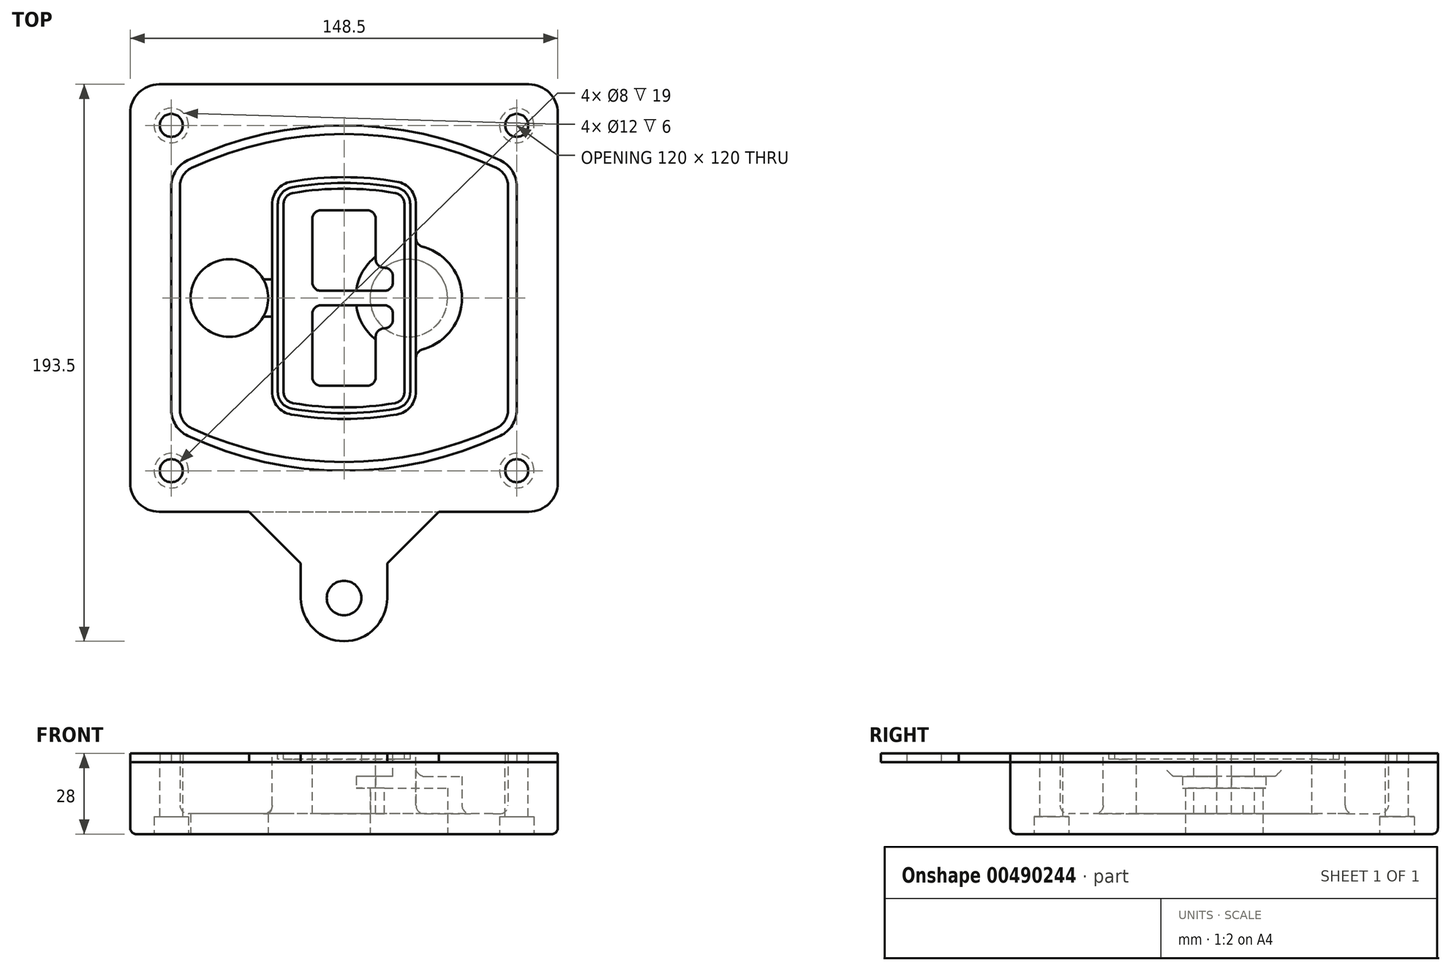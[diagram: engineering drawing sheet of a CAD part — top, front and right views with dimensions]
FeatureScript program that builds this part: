
annotation { "Feature Type Name" : "Feature", "Feature Type Description" : "" }
export const myFeature = defineFeature(function(context is Context, id is Id, definition is map)
    precondition{}
    {
        {
            var Q0;
            Q0=qCreatedBy(makeId("Top.planeOp"),FACE);
            var sketch = newSketch(context, id + "F0", { "sketchPlane" : qUnion([Q0])});
            skPoint(sketch, "E0.rect.middle", {"position": v(0, 0) * mm});
            skLineSegment(sketch, "E1.bottom", {"start": v(-64.25, -74.25) * mm, "end": v(64.25, -74.25) * mm});
            skLineSegment(sketch, "E1.top", {"start": v(-64.25, 74.25) * mm, "end": v(64.25, 74.25) * mm});
            skLineSegment(sketch, "E1.left", {"start": v(-74.25, -64.25) * mm, "end": v(-74.25, 64.25) * mm});
            skLineSegment(sketch, "E1.right", {"start": v(74.25, -64.25) * mm, "end": v(74.25, 64.25) * mm});
            skLineSegment(sketch, "E2", {"start": v(-74.25, 74.25) * mm, "end": v(74.25, -74.25) * mm, "construction": true});
            skLineSegment(sketch, "E3", {"start": v(74.25, 74.25) * mm, "end": v(-74.25, -74.25) * mm, "construction": true});
            skCircle(sketch, "E4", {"center": v(-60, 60) * mm, "radius": 4 * mm});
            skCircle(sketch, "E5", {"center": v(60, 60) * mm, "radius": 4 * mm});
            skCircle(sketch, "E6", {"center": v(60, -60) * mm, "radius": 4 * mm});
            skCircle(sketch, "E7", {"center": v(-60, -60) * mm, "radius": 4 * mm});
            skLineSegment(sketch, "E8", {"start": v(-60, 60) * mm, "end": v(60, 60) * mm, "construction": true});
            skLineSegment(sketch, "E9", {"start": v(60, 60) * mm, "end": v(60, -60) * mm, "construction": true});
            skLineSegment(sketch, "E10", {"start": v(60, -60) * mm, "end": v(-60, -60) * mm, "construction": true});
            skLineSegment(sketch, "E11", {"start": v(-60, -60) * mm, "end": v(-60, 60) * mm, "construction": true});
            skLineSegment(sketch, "E12", {"start": v(-60, 38.83) * mm, "end": v(-60, -38.83) * mm});
            skLineSegment(sketch, "E13", {"start": v(60, 38.83) * mm, "end": v(60, -38.83) * mm});
            skArc(sketch, "E14", {"start": v(54.26, 47.88) * mm, "mid": v(0, 60) * mm, "end": v(-54.26, 47.88) * mm});
            skArc(sketch, "E15", {"start": v(-54.26, -47.88) * mm, "mid": v(0, -60) * mm, "end": v(54.26, -47.88) * mm});
            skLineSegment(sketch, "E16", {"start": v(-60, 0) * mm, "end": v(60, 0) * mm, "construction": true});
            skPoint(sketch, "E17.visualSharp", {"position": v(-60, -45) * mm});
            skArc(sketch, "E17.filletArc", {"start": v(-60, -38.83) * mm, "mid": v(-58.44, -44.2) * mm, "end": v(-54.26, -47.88) * mm});
            skPoint(sketch, "E18.visualSharp", {"position": v(-60, 45) * mm});
            skArc(sketch, "E18.filletArc", {"start": v(-54.26, 47.88) * mm, "mid": v(-58.44, 44.2) * mm, "end": v(-60, 38.83) * mm});
            skPoint(sketch, "E19.visualSharp", {"position": v(60, 45) * mm});
            skArc(sketch, "E19.filletArc", {"start": v(60, 38.83) * mm, "mid": v(58.44, 44.2) * mm, "end": v(54.26, 47.88) * mm});
            skPoint(sketch, "E20.visualSharp", {"position": v(60, -45) * mm});
            skArc(sketch, "E20.filletArc", {"start": v(54.26, -47.88) * mm, "mid": v(58.44, -44.2) * mm, "end": v(60, -38.83) * mm});
            skPoint(sketch, "E21.visualSharp", {"position": v(-74.25, 74.25) * mm});
            skArc(sketch, "E21.filletArc", {"start": v(-64.25, 74.25) * mm, "mid": v(-71.32, 71.32) * mm, "end": v(-74.25, 64.25) * mm});
            skPoint(sketch, "E22.visualSharp", {"position": v(74.25, 74.25) * mm});
            skArc(sketch, "E22.filletArc", {"start": v(74.25, 64.25) * mm, "mid": v(71.32, 71.32) * mm, "end": v(64.25, 74.25) * mm});
            skPoint(sketch, "E23.visualSharp", {"position": v(74.25, -74.25) * mm});
            skArc(sketch, "E23.filletArc", {"start": v(64.25, -74.25) * mm, "mid": v(71.32, -71.32) * mm, "end": v(74.25, -64.25) * mm});
            skPoint(sketch, "E24.visualSharp", {"position": v(-74.25, -74.25) * mm});
            skArc(sketch, "E24.filletArc", {"start": v(-74.25, -64.25) * mm, "mid": v(-71.32, -71.32) * mm, "end": v(-64.25, -74.25) * mm});
            skArc(sketch, "E25.0", {"start": v(57, 38.83) * mm, "mid": v(55.9, 42.58) * mm, "end": v(52.98, 45.17) * mm});
            skLineSegment(sketch, "E25.1", {"start": v(57, 38.83) * mm, "end": v(57, -38.83) * mm});
            skArc(sketch, "E25.2", {"start": v(52.98, -45.17) * mm, "mid": v(55.9, -42.58) * mm, "end": v(57, -38.83) * mm});
            skArc(sketch, "E25.3", {"start": v(-52.98, -45.17) * mm, "mid": v(0, -57) * mm, "end": v(52.98, -45.17) * mm});
            skArc(sketch, "E25.4", {"start": v(-57, -38.83) * mm, "mid": v(-55.9, -42.58) * mm, "end": v(-52.98, -45.17) * mm});
            skArc(sketch, "E25.5", {"start": v(52.98, 45.17) * mm, "mid": v(0, 57) * mm, "end": v(-52.98, 45.17) * mm});
            skLineSegment(sketch, "E25.6", {"start": v(-57, 38.83) * mm, "end": v(-57, -38.83) * mm});
            skArc(sketch, "E25.7", {"start": v(-52.98, 45.17) * mm, "mid": v(-55.9, 42.58) * mm, "end": v(-57, 38.83) * mm});
            skArc(sketch, "E26.0", {"start": v(-55.96, 51.5) * mm, "mid": v(-61.82, 46.33) * mm, "end": v(-64, 38.83) * mm});
            skArc(sketch, "E26.1", {"start": v(55.96, 51.5) * mm, "mid": v(0, 64) * mm, "end": v(-55.96, 51.5) * mm});
            skArc(sketch, "E26.2", {"start": v(64, 38.83) * mm, "mid": v(61.82, 46.33) * mm, "end": v(55.96, 51.5) * mm});
            skLineSegment(sketch, "E26.3", {"start": v(64, 38.83) * mm, "end": v(64, -38.83) * mm});
            skArc(sketch, "E26.4", {"start": v(55.96, -51.5) * mm, "mid": v(61.82, -46.33) * mm, "end": v(64, -38.83) * mm});
            skLineSegment(sketch, "E26.5", {"start": v(-64, 38.83) * mm, "end": v(-64, -38.83) * mm});
            skArc(sketch, "E26.6", {"start": v(-55.96, -51.5) * mm, "mid": v(0, -64) * mm, "end": v(55.96, -51.5) * mm});
            skArc(sketch, "E26.7", {"start": v(-64, -38.83) * mm, "mid": v(-61.82, -46.33) * mm, "end": v(-55.96, -51.5) * mm});
            skSolve(sketch);
        }
        {
            var Q0;
            Q0=makeQuery(id+"F0.imprint","IMPRINT",FACE,{"disambiguationData":[TD([[makeQuery(id+"F0.imprint","IMPRINT",EDGE,{"derivedFrom":sQuery(id+"F0.wireOp",EDGE,"E1.bottom")}),1.0]])]});
            var Q1;
            Q1=makeQuery(id+"F0.imprint","IMPRINT",FACE,{"disambiguationData":[TD([[makeQuery(id+"F0.imprint","IMPRINT",EDGE,{"derivedFrom":sQuery(id+"F0.wireOp",EDGE,"E12")}),1.0]])]});
            var Q2;
            Q2=makeQuery(id+"F0.imprint","IMPRINT",FACE,{"disambiguationData":[TD([[makeQuery(id+"F0.imprint","IMPRINT",EDGE,{"derivedFrom":sQuery(id+"F0.wireOp",EDGE,"E25.0")}),1.0]])]});
            var Q3;
            Q3=makeQuery(id+"F0.imprint","IMPRINT",FACE,{"disambiguationData":[TD([[makeQuery(id+"F0.imprint","IMPRINT",EDGE,{"derivedFrom":sQuery(id+"F0.wireOp",EDGE,"E12")}),-1.0]])]});
            extrude(context, id + "F1", {"entities" : qUnion([Q0, Q1, Q2, Q3]), "oppositeDirection" : true, "depth" : 25 * mm});
        }
        {
            var Q0;
            Q0=makeQuery(id+"F0.imprint","IMPRINT",FACE,{"disambiguationData":[TD([[makeQuery(id+"F0.imprint","IMPRINT",EDGE,{"derivedFrom":sQuery(id+"F0.wireOp",EDGE,"E12")}),1.0]])]});
            extrude(context, id + "F2", {"entities" : qUnion([Q0]), "operationType" : NewBodyOperationType.ADD, "depth" : 3 * mm});
        }
        {
            var Q0;
            Q0=makeQuery(id+"F0.imprint","IMPRINT",FACE,{"disambiguationData":[TD([[makeQuery(id+"F0.imprint","IMPRINT",EDGE,{"derivedFrom":sQuery(id+"F0.wireOp",EDGE,"E25.0")}),1.0]])]});
            extrude(context, id + "F3", {"entities" : qUnion([Q0]), "operationType" : NewBodyOperationType.REMOVE, "oppositeDirection" : true, "depth" : 18 * mm});
        }
        {
            var Q0;
            Q0=makeQuery(id+"F2.opExtrude","CAP_FACE",FACE,{"disambiguationData":[OSD([sQuery(id+"F0.wireOp",EDGE,"E12"),sQuery(id+"F0.wireOp",EDGE,"E13"),sQuery(id+"F0.wireOp",EDGE,"E14"),sQuery(id+"F0.wireOp",EDGE,"E15"),sQuery(id+"F0.wireOp",EDGE,"E17.filletArc"),sQuery(id+"F0.wireOp",EDGE,"E18.filletArc"),sQuery(id+"F0.wireOp",EDGE,"E19.filletArc"),sQuery(id+"F0.wireOp",EDGE,"E20.filletArc"),sQuery(id+"F0.wireOp",EDGE,"E25.0"),sQuery(id+"F0.wireOp",EDGE,"E25.1"),sQuery(id+"F0.wireOp",EDGE,"E25.2"),sQuery(id+"F0.wireOp",EDGE,"E25.3"),sQuery(id+"F0.wireOp",EDGE,"E25.4"),sQuery(id+"F0.wireOp",EDGE,"E25.5"),sQuery(id+"F0.wireOp",EDGE,"E25.6"),sQuery(id+"F0.wireOp",EDGE,"E25.7")])],"isStart":false});
            var sketch = newSketch(context, id + "F4", { "sketchPlane" : qUnion([Q0])});
            skArc(sketch, "E27.0", {"start": v(-18.34, -40.45) * mm, "mid": v(0, -42) * mm, "end": v(18.34, -40.45) * mm});
            skArc(sketch, "E28.0", {"start": v(18.34, 40.45) * mm, "mid": v(0, 42) * mm, "end": v(-18.34, 40.45) * mm});
            skLineSegment(sketch, "E29", {"start": v(-25, 32.57) * mm, "end": v(-25, -32.57) * mm});
            skLineSegment(sketch, "E30", {"start": v(25, 32.57) * mm, "end": v(25, -32.57) * mm});
            skLineSegment(sketch, "E31", {"start": v(-25, 39.1) * mm, "end": v(25, 39.1) * mm, "construction": true});
            skLineSegment(sketch, "E32", {"start": v(-25, -39.1) * mm, "end": v(25, -39.1) * mm, "construction": true});
            skPoint(sketch, "E33.visualSharp", {"position": v(-25, 39.1) * mm});
            skArc(sketch, "E33.filletArc", {"start": v(-18.34, 40.45) * mm, "mid": v(-23.11, 37.73) * mm, "end": v(-25, 32.57) * mm});
            skPoint(sketch, "E34.visualSharp", {"position": v(25, 39.1) * mm});
            skArc(sketch, "E34.filletArc", {"start": v(25, 32.57) * mm, "mid": v(23.11, 37.73) * mm, "end": v(18.34, 40.45) * mm});
            skPoint(sketch, "E35.visualSharp", {"position": v(25, -39.1) * mm});
            skArc(sketch, "E35.filletArc", {"start": v(18.34, -40.45) * mm, "mid": v(23.11, -37.73) * mm, "end": v(25, -32.57) * mm});
            skPoint(sketch, "E36.visualSharp", {"position": v(-25, -39.1) * mm});
            skArc(sketch, "E36.filletArc", {"start": v(-25, -32.57) * mm, "mid": v(-23.11, -37.73) * mm, "end": v(-18.34, -40.45) * mm});
            skArc(sketch, "E37.0", {"start": v(52.98, 45.17) * mm, "mid": v(0, 57) * mm, "end": v(-52.98, 45.17) * mm});
            skArc(sketch, "E37.1", {"start": v(-52.98, 45.17) * mm, "mid": v(-55.9, 42.58) * mm, "end": v(-57, 38.83) * mm});
            skLineSegment(sketch, "E37.2", {"start": v(-57, 38.83) * mm, "end": v(-57, -38.83) * mm});
            skArc(sketch, "E37.3", {"start": v(-57, -38.83) * mm, "mid": v(-55.9, -42.58) * mm, "end": v(-52.98, -45.17) * mm});
            skArc(sketch, "E37.4", {"start": v(-52.98, -45.17) * mm, "mid": v(0, -57) * mm, "end": v(52.98, -45.17) * mm});
            skArc(sketch, "E37.5", {"start": v(52.98, -45.17) * mm, "mid": v(55.9, -42.58) * mm, "end": v(57, -38.83) * mm});
            skLineSegment(sketch, "E37.6", {"start": v(57, 38.83) * mm, "end": v(57, -38.83) * mm});
            skArc(sketch, "E37.7", {"start": v(57, 38.83) * mm, "mid": v(55.9, 42.58) * mm, "end": v(52.98, 45.17) * mm});
            skLineSegment(sketch, "E38.0", {"start": v(23, 32.57) * mm, "end": v(23, -32.57) * mm});
            skArc(sketch, "E38.1", {"start": v(18, -38.48) * mm, "mid": v(21.58, -36.44) * mm, "end": v(23, -32.57) * mm});
            skArc(sketch, "E38.2", {"start": v(-18, -38.48) * mm, "mid": v(0, -40) * mm, "end": v(18, -38.48) * mm});
            skArc(sketch, "E38.3", {"start": v(-23, -32.57) * mm, "mid": v(-21.58, -36.44) * mm, "end": v(-18, -38.48) * mm});
            skLineSegment(sketch, "E38.4", {"start": v(-23, 32.57) * mm, "end": v(-23, -32.57) * mm});
            skArc(sketch, "E38.5", {"start": v(23, 32.57) * mm, "mid": v(21.58, 36.44) * mm, "end": v(18, 38.48) * mm});
            skArc(sketch, "E38.6", {"start": v(-18, 38.48) * mm, "mid": v(-21.58, 36.44) * mm, "end": v(-23, 32.57) * mm});
            skArc(sketch, "E38.7", {"start": v(18, 38.48) * mm, "mid": v(0, 40) * mm, "end": v(-18, 38.48) * mm});
            skArc(sketch, "E39.0", {"start": v(21, 32.57) * mm, "mid": v(20.06, 35.15) * mm, "end": v(17.67, 36.5) * mm});
            skLineSegment(sketch, "E39.1", {"start": v(21, 32.57) * mm, "end": v(21, -32.57) * mm});
            skArc(sketch, "E39.2", {"start": v(17.67, -36.5) * mm, "mid": v(20.06, -35.15) * mm, "end": v(21, -32.57) * mm});
            skArc(sketch, "E39.3", {"start": v(-17.67, -36.5) * mm, "mid": v(0, -38) * mm, "end": v(17.67, -36.5) * mm});
            skArc(sketch, "E39.4", {"start": v(-21, -32.57) * mm, "mid": v(-20.06, -35.15) * mm, "end": v(-17.67, -36.5) * mm});
            skArc(sketch, "E39.5", {"start": v(17.67, 36.5) * mm, "mid": v(0, 38) * mm, "end": v(-17.67, 36.5) * mm});
            skLineSegment(sketch, "E39.6", {"start": v(-21, 32.57) * mm, "end": v(-21, -32.57) * mm});
            skArc(sketch, "E39.7", {"start": v(-17.67, 36.5) * mm, "mid": v(-20.06, 35.15) * mm, "end": v(-21, 32.57) * mm});
            skLineSegment(sketch, "E40", {"start": v(-25, 0) * mm, "end": v(25, 0) * mm, "construction": true});
            skLineSegment(sketch, "E41", {"start": v(-11, 5.5) * mm, "end": v(-11, 27.5) * mm});
            skLineSegment(sketch, "E42", {"start": v(-8, 30.5) * mm, "end": v(8, 30.5) * mm});
            skLineSegment(sketch, "E43", {"start": v(11, 27.5) * mm, "end": v(11, 13.5) * mm});
            skLineSegment(sketch, "E44", {"start": v(14, 10.5) * mm, "end": v(14, 10.5) * mm});
            skLineSegment(sketch, "E45", {"start": v(17, 7.5) * mm, "end": v(17, 5.5) * mm});
            skLineSegment(sketch, "E46", {"start": v(14, 2.5) * mm, "end": v(-8, 2.5) * mm});
            skPoint(sketch, "E47.visualSharp", {"position": v(-11, 30.5) * mm});
            skArc(sketch, "E47.filletArc", {"start": v(-8, 30.5) * mm, "mid": v(-10.12, 29.62) * mm, "end": v(-11, 27.5) * mm});
            skPoint(sketch, "E48.visualSharp", {"position": v(11, 30.5) * mm});
            skArc(sketch, "E48.filletArc", {"start": v(11, 27.5) * mm, "mid": v(10.12, 29.62) * mm, "end": v(8, 30.5) * mm});
            skPoint(sketch, "E49.visualSharp", {"position": v(11, 10.5) * mm});
            skArc(sketch, "E49.filletArc", {"start": v(11, 13.5) * mm, "mid": v(11.88, 11.38) * mm, "end": v(14, 10.5) * mm});
            skPoint(sketch, "E50.visualSharp", {"position": v(17, 10.5) * mm});
            skArc(sketch, "E50.filletArc", {"start": v(17, 7.5) * mm, "mid": v(16.12, 9.62) * mm, "end": v(14, 10.5) * mm});
            skPoint(sketch, "E51.visualSharp", {"position": v(17, 2.5) * mm});
            skArc(sketch, "E51.filletArc", {"start": v(14, 2.5) * mm, "mid": v(16.12, 3.38) * mm, "end": v(17, 5.5) * mm});
            skPoint(sketch, "E52.visualSharp", {"position": v(-11, 2.5) * mm});
            skArc(sketch, "E52.filletArc", {"start": v(-11, 5.5) * mm, "mid": v(-10.12, 3.38) * mm, "end": v(-8, 2.5) * mm});
            skLineSegment(sketch, "E53.0.MirrorCS", {"start": v(14, -2.5) * mm, "end": v(-8, -2.5) * mm});
            skArc(sketch, "E54.0.MirrorCS", {"start": v(-11, -5.5) * mm, "mid": v(-10.12, -3.38) * mm, "end": v(-8, -2.5) * mm});
            skLineSegment(sketch, "E55.0.MirrorCS", {"start": v(-11, -5.5) * mm, "end": v(-11, -27.5) * mm});
            skArc(sketch, "E56.0.MirrorCS", {"start": v(-8, -30.5) * mm, "mid": v(-10.12, -29.62) * mm, "end": v(-11, -27.5) * mm});
            skLineSegment(sketch, "E57.0.MirrorCS", {"start": v(-8, -30.5) * mm, "end": v(8, -30.5) * mm});
            skArc(sketch, "E58.0.MirrorCS", {"start": v(11, -27.5) * mm, "mid": v(10.12, -29.62) * mm, "end": v(8, -30.5) * mm});
            skLineSegment(sketch, "E59.0.MirrorCS", {"start": v(11, -27.5) * mm, "end": v(11, -13.5) * mm});
            skArc(sketch, "E60.0.MirrorCS", {"start": v(11, -13.5) * mm, "mid": v(11.88, -11.38) * mm, "end": v(14, -10.5) * mm});
            skArc(sketch, "E61.0.MirrorCS", {"start": v(17, -7.5) * mm, "mid": v(16.12, -9.62) * mm, "end": v(14, -10.5) * mm});
            skLineSegment(sketch, "E62.0.MirrorCS", {"start": v(17, -7.5) * mm, "end": v(17, -5.5) * mm});
            skArc(sketch, "E63.0.MirrorCS", {"start": v(14, -2.5) * mm, "mid": v(16.12, -3.38) * mm, "end": v(17, -5.5) * mm});
            skSolve(sketch);
        }
        {
            var Q0;
            Q0=makeQuery(id+"F4.imprint","IMPRINT",FACE,{"disambiguationData":[TD([[makeQuery(id+"F4.imprint","IMPRINT",EDGE,{"derivedFrom":sQuery(id+"F4.wireOp",EDGE,"E27.0")}),1.0]])]});
            var Q1;
            Q1=makeQuery(id+"F4.imprint","IMPRINT",FACE,{"disambiguationData":[TD([[makeQuery(id+"F4.imprint","IMPRINT",EDGE,{"derivedFrom":sQuery(id+"F4.wireOp",EDGE,"E38.0")}),-1.0]])]});
            var Q2;
            Q2=makeQuery(id+"F4.imprint","IMPRINT",FACE,{"disambiguationData":[TD([[makeQuery(id+"F4.imprint","IMPRINT",EDGE,{"derivedFrom":sQuery(id+"F4.wireOp",EDGE,"E39.0")}),1.0]])]});
            extrude(context, id + "F5", {"entities" : qUnion([Q0, Q1, Q2]), "operationType" : NewBodyOperationType.ADD, "endBound" : BoundingType.UP_TO_NEXT, "oppositeDirection" : true, "depth" : 25 * mm});
        }
        {
            var Q0;
            Q0=makeQuery(id+"F4.imprint","IMPRINT",FACE,{"disambiguationData":[TD([[makeQuery(id+"F4.imprint","IMPRINT",EDGE,{"derivedFrom":sQuery(id+"F4.wireOp",EDGE,"E38.0")}),-1.0]])]});
            extrude(context, id + "F6", {"entities" : qUnion([Q0]), "operationType" : NewBodyOperationType.REMOVE, "oppositeDirection" : true, "depth" : 2 * mm});
        }
        {
            var Q0;
            Q0=makeQuery(id+"F1.opExtrude","CAP_FACE",FACE,{"disambiguationData":[OSD([sQuery(id+"F0.wireOp",EDGE,"E1.bottom"),sQuery(id+"F0.wireOp",EDGE,"E1.top"),sQuery(id+"F0.wireOp",EDGE,"E1.left"),sQuery(id+"F0.wireOp",EDGE,"E1.right"),sQuery(id+"F0.wireOp",EDGE,"E4"),sQuery(id+"F0.wireOp",EDGE,"E5"),sQuery(id+"F0.wireOp",EDGE,"E6"),sQuery(id+"F0.wireOp",EDGE,"E7"),sQuery(id+"F0.wireOp",EDGE,"E21.filletArc"),sQuery(id+"F0.wireOp",EDGE,"E22.filletArc"),sQuery(id+"F0.wireOp",EDGE,"E23.filletArc"),sQuery(id+"F0.wireOp",EDGE,"E24.filletArc")])],"isStart":false});
            var sketch = newSketch(context, id + "F7", { "sketchPlane" : qUnion([Q0])});
            skCircle(sketch, "E64", {"center": v(22.5, 0) * mm, "radius": 13.47 * mm});
            skCircle(sketch, "E65", {"center": v(-39.81, 0) * mm, "radius": 13.47 * mm});
            skLineSegment(sketch, "E66", {"start": v(74.25, 0) * mm, "end": v(-74.25, 0) * mm});
            skCircle(sketch, "E67", {"center": v(22.5, 0) * mm, "radius": 18.47 * mm});
            skCircle(sketch, "E68", {"center": v(60, -60) * mm, "radius": 6 * mm});
            skCircle(sketch, "E69", {"center": v(-60, -60) * mm, "radius": 6 * mm});
            skCircle(sketch, "E70", {"center": v(-60, 60) * mm, "radius": 6 * mm});
            skCircle(sketch, "E71", {"center": v(60, 60) * mm, "radius": 6 * mm});
            skSolve(sketch);
        }
        {
            var Q0;
            {var subQ1=sQuery(id+"F7.wireOp",EDGE,"E66");var subQ4=sQuery(id+"F7.wireOp",EDGE,"E64");var subQ6=makeQuery(id+"F7.imprint","INTERSECT",VERTEX,{"disambiguationData":[OD(0.0)],"derivedFrom":[subQ4,subQ1]});Q0=makeQuery(id+"F7.imprint","IMPRINT",FACE,{"disambiguationData":[TD([[makeQuery(id+"F7.imprint","IMPRINT",EDGE,{"disambiguationData":[TD([[subQ6,-1.0]])],"derivedFrom":subQ4}),-1.0]])]});}
            var Q1;
            {var subQ0=sQuery(id+"F7.wireOp",EDGE,"E66");var subQ1=sQuery(id+"F7.wireOp",EDGE,"E64");var subQ3=makeQuery(id+"F7.imprint","INTERSECT",VERTEX,{"disambiguationData":[OD(0.0)],"derivedFrom":[subQ1,subQ0]});Q1=makeQuery(id+"F7.imprint","IMPRINT",FACE,{"disambiguationData":[TD([[makeQuery(id+"F7.imprint","IMPRINT",EDGE,{"disambiguationData":[TD([[subQ3,-1.0]])],"derivedFrom":subQ1}),1.0]])]});}
            var Q2;
            {var subQ0=sQuery(id+"F7.wireOp",EDGE,"E66");var subQ1=sQuery(id+"F7.wireOp",EDGE,"E64");var subQ3=makeQuery(id+"F7.imprint","INTERSECT",VERTEX,{"disambiguationData":[OD(0.0)],"derivedFrom":[subQ1,subQ0]});Q2=makeQuery(id+"F7.imprint","IMPRINT",FACE,{"disambiguationData":[TD([[makeQuery(id+"F7.imprint","IMPRINT",EDGE,{"disambiguationData":[TD([[subQ3,1.0]])],"derivedFrom":subQ1}),1.0]])]});}
            var Q3;
            {var subQ1=sQuery(id+"F7.wireOp",EDGE,"E66");var subQ4=sQuery(id+"F7.wireOp",EDGE,"E64");var subQ6=makeQuery(id+"F7.imprint","INTERSECT",VERTEX,{"disambiguationData":[OD(0.0)],"derivedFrom":[subQ4,subQ1]});Q3=makeQuery(id+"F7.imprint","IMPRINT",FACE,{"disambiguationData":[TD([[makeQuery(id+"F7.imprint","IMPRINT",EDGE,{"disambiguationData":[TD([[subQ6,1.0]])],"derivedFrom":subQ4}),-1.0]])]});}
            extrude(context, id + "F8", {"entities" : qUnion([Q0, Q1, Q2, Q3]), "operationType" : NewBodyOperationType.ADD, "oppositeDirection" : true, "depth" : 20 * mm});
        }
        {
            var Q0;
            {var subQ0=sQuery(id+"F7.wireOp",EDGE,"E66");var subQ1=sQuery(id+"F7.wireOp",EDGE,"E64");var subQ3=makeQuery(id+"F7.imprint","INTERSECT",VERTEX,{"disambiguationData":[OD(0.0)],"derivedFrom":[subQ1,subQ0]});Q0=makeQuery(id+"F7.imprint","IMPRINT",FACE,{"disambiguationData":[TD([[makeQuery(id+"F7.imprint","IMPRINT",EDGE,{"disambiguationData":[TD([[subQ3,-1.0]])],"derivedFrom":subQ1}),1.0]])]});}
            var Q1;
            {var subQ0=sQuery(id+"F7.wireOp",EDGE,"E66");var subQ1=sQuery(id+"F7.wireOp",EDGE,"E64");var subQ3=makeQuery(id+"F7.imprint","INTERSECT",VERTEX,{"disambiguationData":[OD(0.0)],"derivedFrom":[subQ1,subQ0]});Q1=makeQuery(id+"F7.imprint","IMPRINT",FACE,{"disambiguationData":[TD([[makeQuery(id+"F7.imprint","IMPRINT",EDGE,{"disambiguationData":[TD([[subQ3,1.0]])],"derivedFrom":subQ1}),1.0]])]});}
            extrude(context, id + "F9", {"entities" : qUnion([Q0, Q1]), "operationType" : NewBodyOperationType.REMOVE, "oppositeDirection" : true, "depth" : 16 * mm});
        }
        {
            var Q0;
            {var subQ0=sQuery(id+"F7.wireOp",EDGE,"E66");var subQ1=sQuery(id+"F7.wireOp",EDGE,"E65");var subQ3=makeQuery(id+"F7.imprint","INTERSECT",VERTEX,{"disambiguationData":[OD(0.0)],"derivedFrom":[subQ1,subQ0]});Q0=makeQuery(id+"F7.imprint","IMPRINT",FACE,{"disambiguationData":[TD([[makeQuery(id+"F7.imprint","IMPRINT",EDGE,{"disambiguationData":[TD([[subQ3,-1.0]])],"derivedFrom":subQ1}),1.0]])]});}
            var Q1;
            {var subQ0=sQuery(id+"F7.wireOp",EDGE,"E66");var subQ1=sQuery(id+"F7.wireOp",EDGE,"E65");var subQ3=makeQuery(id+"F7.imprint","INTERSECT",VERTEX,{"disambiguationData":[OD(0.0)],"derivedFrom":[subQ1,subQ0]});Q1=makeQuery(id+"F7.imprint","IMPRINT",FACE,{"disambiguationData":[TD([[makeQuery(id+"F7.imprint","IMPRINT",EDGE,{"disambiguationData":[TD([[subQ3,1.0]])],"derivedFrom":subQ1}),1.0]])]});}
            extrude(context, id + "F10", {"entities" : qUnion([Q0, Q1]), "operationType" : NewBodyOperationType.REMOVE, "oppositeDirection" : true, "depth" : 25 * mm});
        }
        {
            var Q0;
            Q0=makeQuery(id+"F7.imprint","IMPRINT",FACE,{"disambiguationData":[TD([[makeQuery(id+"F7.imprint","IMPRINT",EDGE,{"derivedFrom":sQuery(id+"F7.wireOp",EDGE,"E68")}),1.0]])]});
            var Q1;
            Q1=makeQuery(id+"F7.imprint","IMPRINT",FACE,{"disambiguationData":[TD([[makeQuery(id+"F7.imprint","IMPRINT",EDGE,{"derivedFrom":makeQuery(id+"F1.opExtrude","CAP_EDGE",EDGE,{"disambiguationData":[OSD([sQuery(id+"F0.wireOp",EDGE,"E5")])],"isStart":false})}),-1.0]])]});
            var Q2;
            Q2=makeQuery(id+"F7.imprint","IMPRINT",FACE,{"disambiguationData":[TD([[makeQuery(id+"F7.imprint","IMPRINT",EDGE,{"derivedFrom":sQuery(id+"F7.wireOp",EDGE,"E69")}),1.0]])]});
            var Q3;
            Q3=makeQuery(id+"F7.imprint","IMPRINT",FACE,{"disambiguationData":[TD([[makeQuery(id+"F7.imprint","IMPRINT",EDGE,{"derivedFrom":makeQuery(id+"F1.opExtrude","CAP_EDGE",EDGE,{"disambiguationData":[OSD([sQuery(id+"F0.wireOp",EDGE,"E4")])],"isStart":false})}),-1.0]])]});
            var Q4;
            Q4=makeQuery(id+"F7.imprint","IMPRINT",FACE,{"disambiguationData":[TD([[makeQuery(id+"F7.imprint","IMPRINT",EDGE,{"derivedFrom":sQuery(id+"F7.wireOp",EDGE,"E70")}),1.0]])]});
            var Q5;
            Q5=makeQuery(id+"F7.imprint","IMPRINT",FACE,{"disambiguationData":[TD([[makeQuery(id+"F7.imprint","IMPRINT",EDGE,{"derivedFrom":makeQuery(id+"F1.opExtrude","CAP_EDGE",EDGE,{"disambiguationData":[OSD([sQuery(id+"F0.wireOp",EDGE,"E7")])],"isStart":false})}),-1.0]])]});
            var Q6;
            Q6=makeQuery(id+"F7.imprint","IMPRINT",FACE,{"disambiguationData":[TD([[makeQuery(id+"F7.imprint","IMPRINT",EDGE,{"derivedFrom":sQuery(id+"F7.wireOp",EDGE,"E71")}),1.0]])]});
            var Q7;
            Q7=makeQuery(id+"F7.imprint","IMPRINT",FACE,{"disambiguationData":[TD([[makeQuery(id+"F7.imprint","IMPRINT",EDGE,{"derivedFrom":makeQuery(id+"F1.opExtrude","CAP_EDGE",EDGE,{"disambiguationData":[OSD([sQuery(id+"F0.wireOp",EDGE,"E6")])],"isStart":false})}),-1.0]])]});
            extrude(context, id + "F11", {"entities" : qUnion([Q0, Q1, Q2, Q3, Q4, Q5, Q6, Q7]), "operationType" : NewBodyOperationType.REMOVE, "oppositeDirection" : true, "depth" : 6 * mm});
        }
        {
            var Q0;
            Q0=makeQuery(id+"F9.boolean.opBoolean","COPY",FACE,{"derivedFrom":makeQuery(id+"F9.opExtrude","CAP_FACE",FACE,{"disambiguationData":[OSD([sQuery(id+"F7.wireOp",EDGE,"E64")])],"isStart":false})});
            var sketch = newSketch(context, id + "F12", { "sketchPlane" : qUnion([Q0])});
            skArc(sketch, "E72.0", {"start": v(11, 14.45) * mm, "mid": v(6.45, 9.13) * mm, "end": v(4.2, 2.5) * mm});
            skArc(sketch, "E72.1", {"start": v(4.2, -2.5) * mm, "mid": v(6.45, -9.13) * mm, "end": v(11, -14.45) * mm});
            skLineSegment(sketch, "E73", {"start": v(4.2, -2.5) * mm, "end": v(14, -2.5) * mm});
            skLineSegment(sketch, "E74.0", {"start": v(14, 2.5) * mm, "end": v(4.2, 2.5) * mm});
            skArc(sketch, "E74.1", {"start": v(14, 2.5) * mm, "mid": v(16.12, 3.38) * mm, "end": v(17, 5.5) * mm});
            skLineSegment(sketch, "E74.2", {"start": v(17, 7.5) * mm, "end": v(17, 5.5) * mm});
            skArc(sketch, "E74.3", {"start": v(17, 7.5) * mm, "mid": v(16.12, 9.62) * mm, "end": v(14, 10.5) * mm});
            skArc(sketch, "E74.4", {"start": v(11, 13.5) * mm, "mid": v(11.88, 11.38) * mm, "end": v(14, 10.5) * mm});
            skLineSegment(sketch, "E74.5", {"start": v(11, 14.45) * mm, "end": v(11, 13.5) * mm});
            skLineSegment(sketch, "E74.7", {"start": v(14, -2.5) * mm, "end": v(4.2, -2.5) * mm});
            skArc(sketch, "E74.8", {"start": v(14, -2.5) * mm, "mid": v(16.12, -3.38) * mm, "end": v(17, -5.5) * mm});
            skLineSegment(sketch, "E74.9", {"start": v(17, -7.5) * mm, "end": v(17, -5.5) * mm});
            skArc(sketch, "E74.10", {"start": v(17, -7.5) * mm, "mid": v(16.12, -9.62) * mm, "end": v(14, -10.5) * mm});
            skArc(sketch, "E74.11", {"start": v(11, -13.5) * mm, "mid": v(11.88, -11.38) * mm, "end": v(14, -10.5) * mm});
            skLineSegment(sketch, "E74.12", {"start": v(11, -14.45) * mm, "end": v(11, -13.5) * mm});
            skPoint(sketch, "E75.orphan", {"position": v(11, -27.5) * mm});
            skPoint(sketch, "E76.orphan", {"position": v(-8, -2.5) * mm});
            skPoint(sketch, "E77.orphan", {"position": v(-8, 2.5) * mm});
            skPoint(sketch, "E78.orphan", {"position": v(11, 27.5) * mm});
            skSolve(sketch);
        }
        {
            var Q0;
            {var subQ7=sQuery(id+"F12.wireOp",EDGE,"E72.0");var subQ14=sQuery(id+"F12.wireOp",EDGE,"E72.1");var subQ16=sQuery(id+"F12.wireOp",EDGE,"E74.1");var subQ18=sQuery(id+"F12.wireOp",EDGE,"E74.8");Q0=qUnion([makeQuery(id+"F12.imprint","IMPRINT",FACE,{"disambiguationData":[TD([[makeQuery(id+"F12.imprint","IMPRINT",EDGE,{"derivedFrom":subQ7}),1.0]])]}),makeQuery(id+"F12.imprint","IMPRINT",FACE,{"disambiguationData":[TD([[makeQuery(id+"F12.imprint","IMPRINT",EDGE,{"derivedFrom":subQ14}),1.0]])]}),makeQuery(id+"F12.imprint","IMPRINT",FACE,{"disambiguationData":[TD([[makeQuery(id+"F12.imprint","IMPRINT",EDGE,{"derivedFrom":subQ16}),1.0]])]}),makeQuery(id+"F12.imprint","IMPRINT",FACE,{"disambiguationData":[TD([[makeQuery(id+"F12.imprint","IMPRINT",EDGE,{"derivedFrom":subQ18}),-1.0]])]})]);}
            var Q1;
            Q1=makeQuery(id+"F5.boolean.opBoolean","SPLIT",FACE,{"disambiguationData":[TD([makeQuery(id+"F5.opExtrude","SWEPT_FACE",FACE,{"disambiguationData":[OSD([sQuery(id+"F4.wireOp",EDGE,"E41")])]})])],"derivedFrom":makeQuery(id+"F3.boolean.opBoolean","COPY",FACE,{"derivedFrom":makeQuery(id+"F3.opExtrude","CAP_FACE",FACE,{"disambiguationData":[OSD([sQuery(id+"F0.wireOp",EDGE,"E25.0"),sQuery(id+"F0.wireOp",EDGE,"E25.1"),sQuery(id+"F0.wireOp",EDGE,"E25.2"),sQuery(id+"F0.wireOp",EDGE,"E25.3"),sQuery(id+"F0.wireOp",EDGE,"E25.4"),sQuery(id+"F0.wireOp",EDGE,"E25.5"),sQuery(id+"F0.wireOp",EDGE,"E25.6"),sQuery(id+"F0.wireOp",EDGE,"E25.7")])],"isStart":false})})});
            extrude(context, id + "F13", {"entities" : qUnion([Q0]), "operationType" : NewBodyOperationType.REMOVE, "endBound" : BoundingType.UP_TO_SURFACE, "endBoundEntityFace" : qUnion([Q1]), "depth" : 25 * mm});
        }
        {
            var Q0;
            Q0=makeQuery(id+"F3.boolean.opBoolean","COPY",EDGE,{"derivedFrom":makeQuery(id+"F3.opExtrude","CAP_EDGE",EDGE,{"disambiguationData":[OSD([sQuery(id+"F0.wireOp",EDGE,"E25.6")])],"isStart":false})});
            var Q1;
            Q1=makeQuery(id+"F8.boolean.opBoolean","INTERSECT",EDGE,{"derivedFrom":[makeQuery(id+"F5.opExtrude","SWEPT_FACE",FACE,{"disambiguationData":[OSD([sQuery(id+"F4.wireOp",EDGE,"E30")])]}),makeQuery(id+"F8.opExtrude","CAP_FACE",FACE,{"disambiguationData":[OSD([sQuery(id+"F7.wireOp",EDGE,"E67")])],"isStart":false})]});
            var Q2;
            Q2=makeQuery(id+"F8.boolean.opBoolean","INTERSECT",EDGE,{"disambiguationData":[OD(1.0)],"derivedFrom":[makeQuery(id+"F5.opExtrude","SWEPT_FACE",FACE,{"disambiguationData":[OSD([sQuery(id+"F4.wireOp",EDGE,"E30")])]}),makeQuery(id+"F8.opExtrude","SWEPT_FACE",FACE,{"disambiguationData":[OSD([sQuery(id+"F7.wireOp",EDGE,"E67")])]})]});
            var Q3;
            {var subQ0=sQuery(id+"F4.wireOp",EDGE,"E30");Q3=makeQuery(id+"F8.boolean.opBoolean","SPLIT",EDGE,{"disambiguationData":[TD([makeQuery(id+"F5.opExtrude","SWEPT_FACE",FACE,{"disambiguationData":[OSD([sQuery(id+"F4.wireOp",EDGE,"E35.filletArc")])]})])],"derivedFrom":makeQuery(id+"F5.opExtrude","CAP_EDGE",EDGE,{"disambiguationData":[OSD([subQ0])],"isStart":false})});}
            var Q4;
            {var subQ0=sQuery(id+"F0.wireOp",EDGE,"E25.7");var subQ1=sQuery(id+"F0.wireOp",EDGE,"E25.1");var subQ2=sQuery(id+"F0.wireOp",EDGE,"E25.6");var subQ3=sQuery(id+"F0.wireOp",EDGE,"E25.5");var subQ4=sQuery(id+"F0.wireOp",EDGE,"E25.4");var subQ5=sQuery(id+"F0.wireOp",EDGE,"E25.0");var subQ6=sQuery(id+"F0.wireOp",EDGE,"E25.2");var subQ7=sQuery(id+"F0.wireOp",EDGE,"E25.3");Q4=makeQuery(id+"F8.boolean.opBoolean","INTERSECT",EDGE,{"derivedFrom":[makeQuery(id+"F5.boolean.opBoolean","SPLIT",FACE,{"disambiguationData":[TD([makeQuery(id+"F2.opExtrude","SWEPT_FACE",FACE,{"disambiguationData":[OSD([subQ5])]})])],"derivedFrom":makeQuery(id+"F3.boolean.opBoolean","COPY",FACE,{"derivedFrom":makeQuery(id+"F3.opExtrude","CAP_FACE",FACE,{"disambiguationData":[OSD([subQ5,subQ1,subQ6,subQ7,subQ4,subQ3,subQ2,subQ0])],"isStart":false})})}),makeQuery(id+"F8.opExtrude","SWEPT_FACE",FACE,{"disambiguationData":[OSD([sQuery(id+"F7.wireOp",EDGE,"E67")])]})]});}
            var Q5;
            Q5=makeQuery(id+"F8.boolean.opBoolean","INTERSECT",EDGE,{"disambiguationData":[OD(0.0)],"derivedFrom":[makeQuery(id+"F5.opExtrude","SWEPT_FACE",FACE,{"disambiguationData":[OSD([sQuery(id+"F4.wireOp",EDGE,"E30")])]}),makeQuery(id+"F8.opExtrude","SWEPT_FACE",FACE,{"disambiguationData":[OSD([sQuery(id+"F7.wireOp",EDGE,"E67")])]})]});
            fillet(context, id + "F14", {"entities" : qUnion([Q0, Q1, Q2, Q3, Q4, Q5]), "radius" : 3 * mm, "tangentPropagation" : true, "allowEdgeOverflow" : false});
        }
        {
            var Q0;
            Q0=makeQuery(id+"F1.opExtrude","CAP_EDGE",EDGE,{"disambiguationData":[OSD([sQuery(id+"F0.wireOp",EDGE,"E1.bottom")])],"isStart":false});
            fillet(context, id + "F15", {"entities" : qUnion([Q0]), "radius" : 2 * mm, "tangentPropagation" : true, "allowEdgeOverflow" : false});
        }
        {
            var Q0;
            {var subQ0=sQuery(id+"F0.wireOp",EDGE,"E21.filletArc");var subQ1=sQuery(id+"F0.wireOp",EDGE,"E7");var subQ2=sQuery(id+"F0.wireOp",EDGE,"E6");var subQ3=sQuery(id+"F0.wireOp",EDGE,"E5");var subQ4=sQuery(id+"F0.wireOp",EDGE,"E4");var subQ5=sQuery(id+"F0.wireOp",EDGE,"E22.filletArc");var subQ6=sQuery(id+"F0.wireOp",EDGE,"E1.bottom");var subQ7=sQuery(id+"F0.wireOp",EDGE,"E1.right");var subQ8=sQuery(id+"F0.wireOp",EDGE,"E1.top");var subQ9=sQuery(id+"F0.wireOp",EDGE,"E1.left");var subQ10=sQuery(id+"F0.wireOp",EDGE,"E23.filletArc");var subQ11=sQuery(id+"F0.wireOp",EDGE,"E24.filletArc");Q0=makeQuery(id+"F2.boolean.opBoolean","SPLIT",FACE,{"disambiguationData":[TD([makeQuery(id+"F1.opExtrude","SWEPT_FACE",FACE,{"disambiguationData":[OSD([subQ6])]})])],"derivedFrom":makeQuery(id+"F1.opExtrude","CAP_FACE",FACE,{"disambiguationData":[OSD([subQ6,subQ8,subQ9,subQ7,subQ4,subQ3,subQ2,subQ1,subQ0,subQ5,subQ10,subQ11])],"isStart":true})});}
            var sketch = newSketch(context, id + "F16", { "sketchPlane" : qUnion([Q0])});
            skLineSegment(sketch, "E79", {"start": v(0, 74.25) * mm, "end": v(0, 104.25) * mm, "construction": true});
            skArc(sketch, "E80", {"start": v(15, 104.25) * mm, "mid": v(0, 119.25) * mm, "end": v(-15, 104.25) * mm});
            skLineSegment(sketch, "E81", {"start": v(15, 104.25) * mm, "end": v(15, 92.25) * mm});
            skLineSegment(sketch, "E82", {"start": v(-15, 104.25) * mm, "end": v(-15, 92.25) * mm});
            skLineSegment(sketch, "E83", {"start": v(15, 92.25) * mm, "end": v(33, 74.25) * mm});
            skLineSegment(sketch, "E84", {"start": v(-15, 92.25) * mm, "end": v(-33, 74.25) * mm});
            skCircle(sketch, "E85", {"center": v(0, 104.25) * mm, "radius": 6 * mm});
            skLineSegment(sketch, "E86", {"start": v(-74.25, 0) * mm, "end": v(74.25, 0) * mm, "construction": true});
            skArc(sketch, "E87.MirrorCS", {"start": v(-15, 104.25) * mm, "mid": v(0, 119.25) * mm, "end": v(15, 104.25) * mm});
            skArc(sketch, "E88.MirrorCS", {"start": v(15, -104.25) * mm, "mid": v(0, -119.25) * mm, "end": v(-15, -104.25) * mm});
            skLineSegment(sketch, "E89.MirrorCS", {"start": v(15, -104.25) * mm, "end": v(15, -92.25) * mm});
            skLineSegment(sketch, "E90.MirrorCS", {"start": v(-15, -104.25) * mm, "end": v(-15, -92.25) * mm});
            skLineSegment(sketch, "E91.MirrorCS", {"start": v(15, -92.25) * mm, "end": v(33, -74.25) * mm});
            skLineSegment(sketch, "E92.MirrorCS", {"start": v(-15, -92.25) * mm, "end": v(-33, -74.25) * mm});
            skCircle(sketch, "E93.MirrorC", {"center": v(0, -104.25) * mm, "radius": 6 * mm});
            skArc(sketch, "E94.MirrorCS", {"start": v(-15, -104.25) * mm, "mid": v(0, -119.25) * mm, "end": v(15, -104.25) * mm});
            skLineSegment(sketch, "E95.MirrorCS", {"start": v(0, -74.25) * mm, "end": v(0, -104.25) * mm, "construction": true});
            skSolve(sketch);
        }
        {
            var Q0;
            Q0=makeQuery(id+"F16.imprint","IMPRINT",FACE,{"disambiguationData":[TD([[makeQuery(id+"F16.imprint","IMPRINT",EDGE,{"derivedFrom":sQuery(id+"F16.wireOp",EDGE,"E87.MirrorCS")}),-1.0]])]});
            var Q1;
            Q1=makeQuery(id+"F16.imprint","IMPRINT",FACE,{"disambiguationData":[TD([[makeQuery(id+"F16.imprint","IMPRINT",EDGE,{"derivedFrom":makeQuery(id+"F1.opExtrude","CAP_EDGE",EDGE,{"disambiguationData":[OSD([sQuery(id+"F0.wireOp",EDGE,"E1.left")])],"isStart":true})}),-1.0]])]});
            var Q2;
            {var subQ1=sQuery(id+"F16.wireOp",EDGE,"E92.MirrorCS");Q2=makeQuery(id+"F16.imprint","IMPRINT",FACE,{"disambiguationData":[TD([[makeQuery(id+"F16.imprint","IMPRINT",EDGE,{"derivedFrom":subQ1}),-1.0]])]});}
            var Q3;
            Q3=makeQuery(id+"F2.opExtrude","CAP_FACE",FACE,{"disambiguationData":[OSD([sQuery(id+"F0.wireOp",EDGE,"E12"),sQuery(id+"F0.wireOp",EDGE,"E13"),sQuery(id+"F0.wireOp",EDGE,"E14"),sQuery(id+"F0.wireOp",EDGE,"E15"),sQuery(id+"F0.wireOp",EDGE,"E17.filletArc"),sQuery(id+"F0.wireOp",EDGE,"E18.filletArc"),sQuery(id+"F0.wireOp",EDGE,"E19.filletArc"),sQuery(id+"F0.wireOp",EDGE,"E20.filletArc"),sQuery(id+"F0.wireOp",EDGE,"E25.0"),sQuery(id+"F0.wireOp",EDGE,"E25.1"),sQuery(id+"F0.wireOp",EDGE,"E25.2"),sQuery(id+"F0.wireOp",EDGE,"E25.3"),sQuery(id+"F0.wireOp",EDGE,"E25.4"),sQuery(id+"F0.wireOp",EDGE,"E25.5"),sQuery(id+"F0.wireOp",EDGE,"E25.6"),sQuery(id+"F0.wireOp",EDGE,"E25.7")])],"isStart":false});
            extrude(context, id + "F17", {"entities" : qUnion([Q0, Q1, Q2]), "endBound" : BoundingType.UP_TO_SURFACE, "endBoundEntityFace" : qUnion([Q3]), "depth" : 25 * mm});
        }
    });
